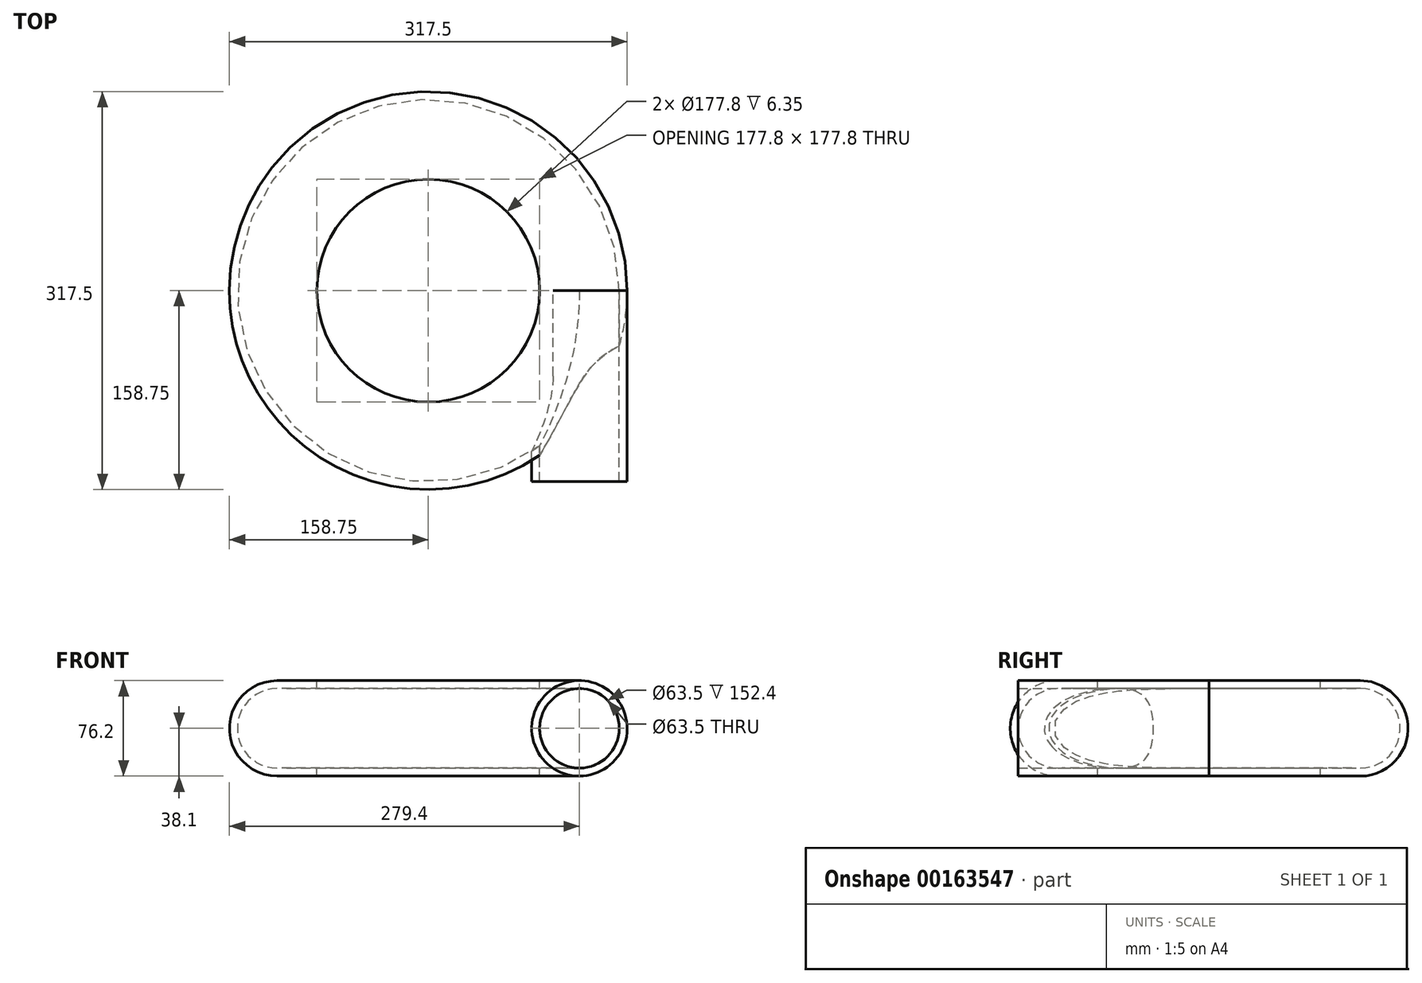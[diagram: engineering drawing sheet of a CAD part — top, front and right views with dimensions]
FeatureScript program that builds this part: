
annotation { "Feature Type Name" : "Feature", "Feature Type Description" : "" }
export const myFeature = defineFeature(function(context is Context, id is Id, definition is map)
    precondition{}
    {
        {
            var Q0;
            Q0=qCreatedBy(makeId("Front.planeOp"),FACE);
            var sketch = newSketch(context, id + "F0", { "sketchPlane" : qUnion([Q0])});
            skLineSegment(sketch, "E0", {"start": v(0, 31.75) * mm, "end": v(120.65, 31.75) * mm});
            skArc(sketch, "E1", {"start": v(120.65, 31.75) * mm, "mid": v(143.1, 22.45) * mm, "end": v(152.4, 0) * mm});
            skLineSegment(sketch, "E2.MirrorCS", {"start": v(0, -31.75) * mm, "end": v(120.65, -31.75) * mm});
            skArc(sketch, "E3.MirrorCS", {"start": v(120.65, -31.75) * mm, "mid": v(143.1, -22.45) * mm, "end": v(152.4, 0) * mm});
            skLineSegment(sketch, "E4.0", {"start": v(0, 38.1) * mm, "end": v(120.65, 38.1) * mm});
            skArc(sketch, "E4.1", {"start": v(120.65, 38.1) * mm, "mid": v(147.6, 26.94) * mm, "end": v(158.75, 0) * mm});
            skArc(sketch, "E4.2", {"start": v(120.65, -38.1) * mm, "mid": v(147.6, -26.94) * mm, "end": v(158.75, 0) * mm});
            skLineSegment(sketch, "E4.3", {"start": v(0, -38.1) * mm, "end": v(120.65, -38.1) * mm});
            skLineSegment(sketch, "E5", {"start": v(0, 31.75) * mm, "end": v(0, 38.1) * mm});
            skLineSegment(sketch, "E6", {"start": v(0, -31.75) * mm, "end": v(0, -38.1) * mm});
            skLineSegment(sketch, "E7", {"start": v(0, 31.75) * mm, "end": v(0, -31.75) * mm});
            skSolve(sketch);
        }
        {
            var Q0;
            Q0 = qSketchRegion(id + "F0", true);
            var Q1;
            Q1=sQuery(id+"F0.wireOp",EDGE,"E5");
            revolve(context, id + "F1", {"entities" : qUnion([Q0]), "axis" : qUnion([Q1]), "revolveType" : RevolveType.FULL});
        }
        {
            var Q0;
            Q0=makeQuery(id+"F1.opRevolve","SWEPT_FACE",FACE,{"disambiguationData":[OSD([sQuery(id+"F0.wireOp",EDGE,"E4.0")])]});
            var sketch = newSketch(context, id + "F2", { "sketchPlane" : qUnion([Q0])});
            skCircle(sketch, "E8", {"center": v(0, 0) * mm, "radius": 88.9 * mm});
            skSolve(sketch);
        }
        {
            var Q0;
            Q0 = qSketchRegion(id + "F2", true);
            extrude(context, id + "F3", {"entities" : qUnion([Q0]), "operationType" : NewBodyOperationType.REMOVE, "oppositeDirection" : true, "depth" : 76.2 * mm});
        }
        {
            var Q0;
            Q0=qCreatedBy(makeId("Front.planeOp"),FACE);
            var sketch = newSketch(context, id + "F4", { "sketchPlane" : qUnion([Q0])});
            skCircle(sketch, "E9", {"center": v(120.65, 0) * mm, "radius": 31.75 * mm});
            skCircle(sketch, "E10.0", {"center": v(120.65, 0) * mm, "radius": 38.1 * mm});
            skSolve(sketch);
        }
        {
            var Q0;
            Q0 = qSketchRegion(id + "F4", true);
            extrude(context, id + "F5", {"entities" : qUnion([Q0]), "depth" : 152.4 * mm});
        }
        {
            var Q0;
            Q0=makeQuery(id+"F5.opExtrude","CAP_FACE",FACE,{"disambiguationData":[OSD([sQuery(id+"F4.wireOp",EDGE,"E9"),sQuery(id+"F4.wireOp",EDGE,"E10.0")])],"isStart":false});
            var sketch = newSketch(context, id + "F6", { "sketchPlane" : qUnion([Q0])});
            skCircle(sketch, "E11", {"center": v(120.65, 0) * mm, "radius": 31.75 * mm});
            skSolve(sketch);
        }
        {
            var Q0;
            Q0=makeQuery(id+"F0.imprint","IMPRINT",FACE,{"disambiguationData":[TD([[makeQuery(id+"F0.imprint","IMPRINT",EDGE,{"derivedFrom":sQuery(id+"F0.wireOp",EDGE,"E0")}),-1.0]])]});
            var Q1;
            Q1=sQuery(id+"F0.wireOp",EDGE,"E7");
            revolve(context, id + "F7", {"operationType" : NewBodyOperationType.REMOVE, "entities" : qUnion([Q0]), "axis" : qUnion([Q1]), "revolveType" : RevolveType.FULL, "oppositeDirection" : true});
        }
        {
            var Q0;
            Q0 = qSketchRegion(id + "F6", true);
            extrude(context, id + "F8", {"entities" : qUnion([Q0]), "operationType" : NewBodyOperationType.REMOVE, "oppositeDirection" : true, "depth" : 152.4 * mm});
        }
    });
